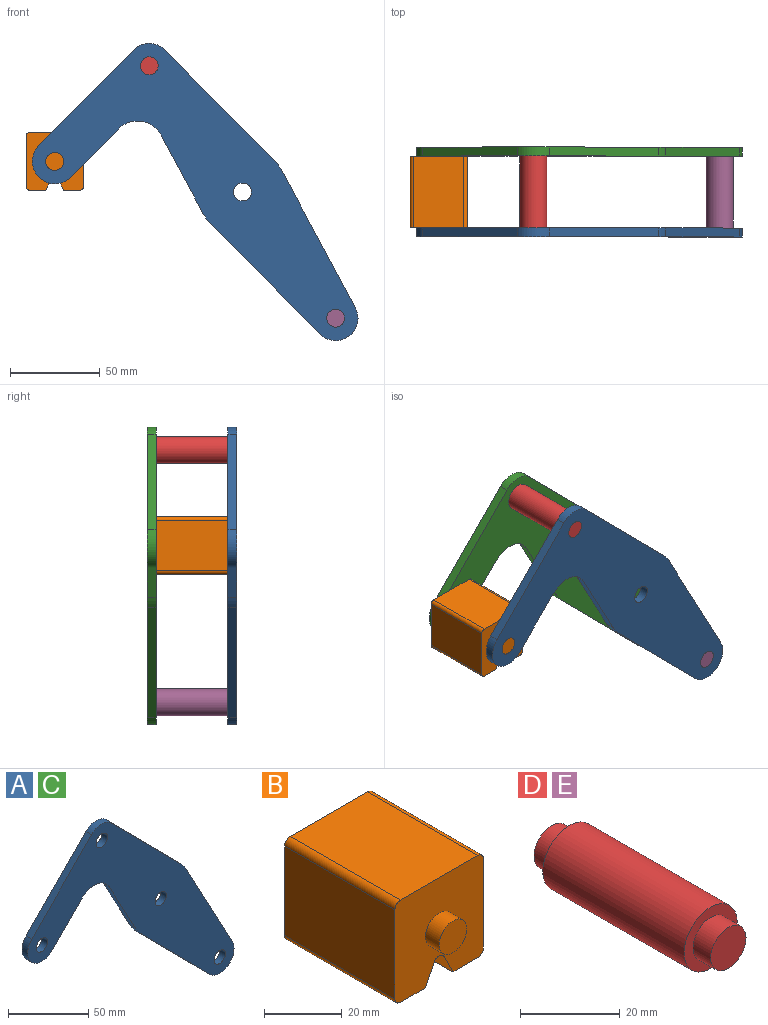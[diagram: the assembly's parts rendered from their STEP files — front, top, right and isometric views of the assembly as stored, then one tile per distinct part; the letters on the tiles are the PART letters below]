
ASSEMBLY  parts=5 mates=3
PART A: 18 faces, bbox 181.7x5x165.8 mm
  f0: plane 43.49x23.35mm, normal (-0.88,0,-0.47), area 246.8mm2, adj f1,f14,f16,f17
  f1: cylinder r=25mm len=5.75mm, axis (0,1,0), area 35.8mm2, adj f0,f2,f16,f17
  f2: plane 61.6x60.87mm, normal (-0.71,0,-0.7), area 433mm2, adj f1,f3,f16,f17
  f3: cylinder r=12.5mm len=21.39mm, axis (0,1,0), area 178.4mm2, adj f2,f4,f16,f17
  f4: plane 76.3x40.96mm, normal (0.88,0,0.47), area 433mm2, adj f3,f5,f16,f17
  f5: cylinder r=25mm len=5.75mm, axis (0,1,0), area 35.8mm2, adj f4,f6,f16,f17
  f6: plane 61.6x60.87mm, normal (0.71,0,0.7), area 433mm2, adj f5,f7,f16,f17
  f7: cylinder r=12.5mm len=17.78mm, axis (0,1,0), area 98.9mm2, adj f6,f8,f16,f17
  f8: plane 53.35x52.71mm, normal (-0.71,0,0.7), area 375mm2, adj f7,f9,f16,f17
  f9: cylinder r=12.5mm len=21.39mm, axis (0,1,0), area 196.3mm2, adj f8,f10,f16,f17
  f10: plane 26.86x26.54mm, normal (0.71,0,-0.7), area 188.8mm2, adj f9,f14,f16,f17
  f11: cylinder r=5mm len=10mm, axis (0,1,0), area 157.1mm2, adj f16,f17
  f12: cylinder r=5mm len=10mm, axis (0,1,0), area 157.1mm2, adj f16,f17
  f13: cylinder r=5mm len=10mm, axis (0,1,0), area 157.1mm2, adj f16,f17
  f14: cylinder r=15mm len=23.89mm, axis (0,1,0), area 140.2mm2, adj f0,f10,f16,f17
  f15: cylinder r=5mm len=10mm, axis (0,1,0), area 157.1mm2, adj f16,f17
  f16: plane 181.66x165.78mm, normal (0,-1,0), area 8710.1mm2, adj f0,f1,f2,f3,f4,f5,f6,f7
  f17: plane 181.66x165.78mm, normal (0,1,0), area 8710.1mm2, adj f0,f1,f2,f3,f4,f5,f6,f7
PART B: 18 faces, bbox 32.1x50x32.1 mm
  f0: plane 40x28.08mm, normal (1,0,0), area 1123.1mm2, adj f4,f10,f13,f14
  f1: plane 40x9.04mm, normal (0,0,-1), area 361.6mm2, adj f2,f4,f10,f14
  f2: plane 40x6.42mm, normal (-0.89,0,-0.45), area 287.2mm2, adj f1,f4,f10,f15
  f3: plane 40x6.42mm, normal (0.89,0,-0.45), area 287.2mm2, adj f4,f5,f10,f15
  f4: plane 32.08x32.08mm, normal (0,-1,0), area 900.6mm2, adj f0,f1,f2,f3,f5,f6,f7,f9
  f5: plane 40x9.04mm, normal (0,0,-1), area 361.6mm2, adj f3,f4,f10,f16
  f6: plane 40x28.08mm, normal (0,0,1), area 1123.1mm2, adj f4,f10,f13,f17
  f7: plane 40x28.08mm, normal (-1,0,0), area 1123.1mm2, adj f4,f10,f16,f17
  f8: plane 10x10mm, normal (0,-1,0), area 78.5mm2, adj f9
  f9: cylinder r=5mm len=10mm, axis (0,1,0), area 157.1mm2, adj f4,f8
  f10: plane 32.08x32.08mm, normal (0,1,0), area 900.6mm2, adj f0,f1,f2,f3,f5,f6,f7,f12
  f11: plane 10x10mm, normal (0,1,0), area 78.5mm2, adj f12
  f12: cylinder r=5mm len=10mm, axis (0,-1,0), area 157.1mm2, adj f10,f11
  f13: cylinder r=2mm len=40mm, axis (0,1,0), area 125.7mm2, adj f0,f4,f6,f10
  f14: cylinder r=2mm len=40mm, axis (0,-1,0), area 125.7mm2, adj f0,f1,f4,f10
  f15: cylinder r=2mm len=40mm, axis (0,1,0), area 177.1mm2, adj f2,f3,f4,f10
  f16: cylinder r=2mm len=40mm, axis (0,1,0), area 125.7mm2, adj f4,f5,f7,f10
  f17: cylinder r=2mm len=40mm, axis (0,-1,0), area 125.7mm2, adj f4,f6,f7,f10
PART C: same geometry as A
PART D: 7 faces, bbox 15x50x15 mm
  f0: cylinder r=7.5mm len=40mm, axis (0,-1,0), area 1885mm2, adj f2,f5
  f1: cylinder r=5mm len=10mm, axis (0,1,0), area 157.1mm2, adj f2,f3
  f2: plane 15x15mm, normal (0,-1,0), area 98.2mm2, adj f0,f1
  f3: plane 10x10mm, normal (0,-1,0), area 78.5mm2, adj f1
  f4: cylinder r=5mm len=10mm, axis (0,-1,0), area 157.1mm2, adj f5,f6
  f5: plane 15x15mm, normal (0,1,0), area 98.2mm2, adj f0,f4
  f6: plane 10x10mm, normal (0,1,0), area 78.5mm2, adj f4
PART E: same geometry as D
PLACE A t=(0,-20,0)mm fixed
PLACE B t=(0,-20,0)mm
PLACE C t=(0,25,0)mm
PLACE D t=(0,-20,0)mm
PLACE E t=(103.95,-20,-140.78)mm
MATE fastened E.f0 <-> A.f3  axis (0,-1,0) through (51.98,-20,-70.39)mm
MATE revolute B.f9 <-> A.f9  axis (0,-1,0) through (-104.69,-20,17.04)mm
MATE fastened D.f0 <-> C.f7  axis (0,-1,0) through (-51.98,20,70.39)mm
